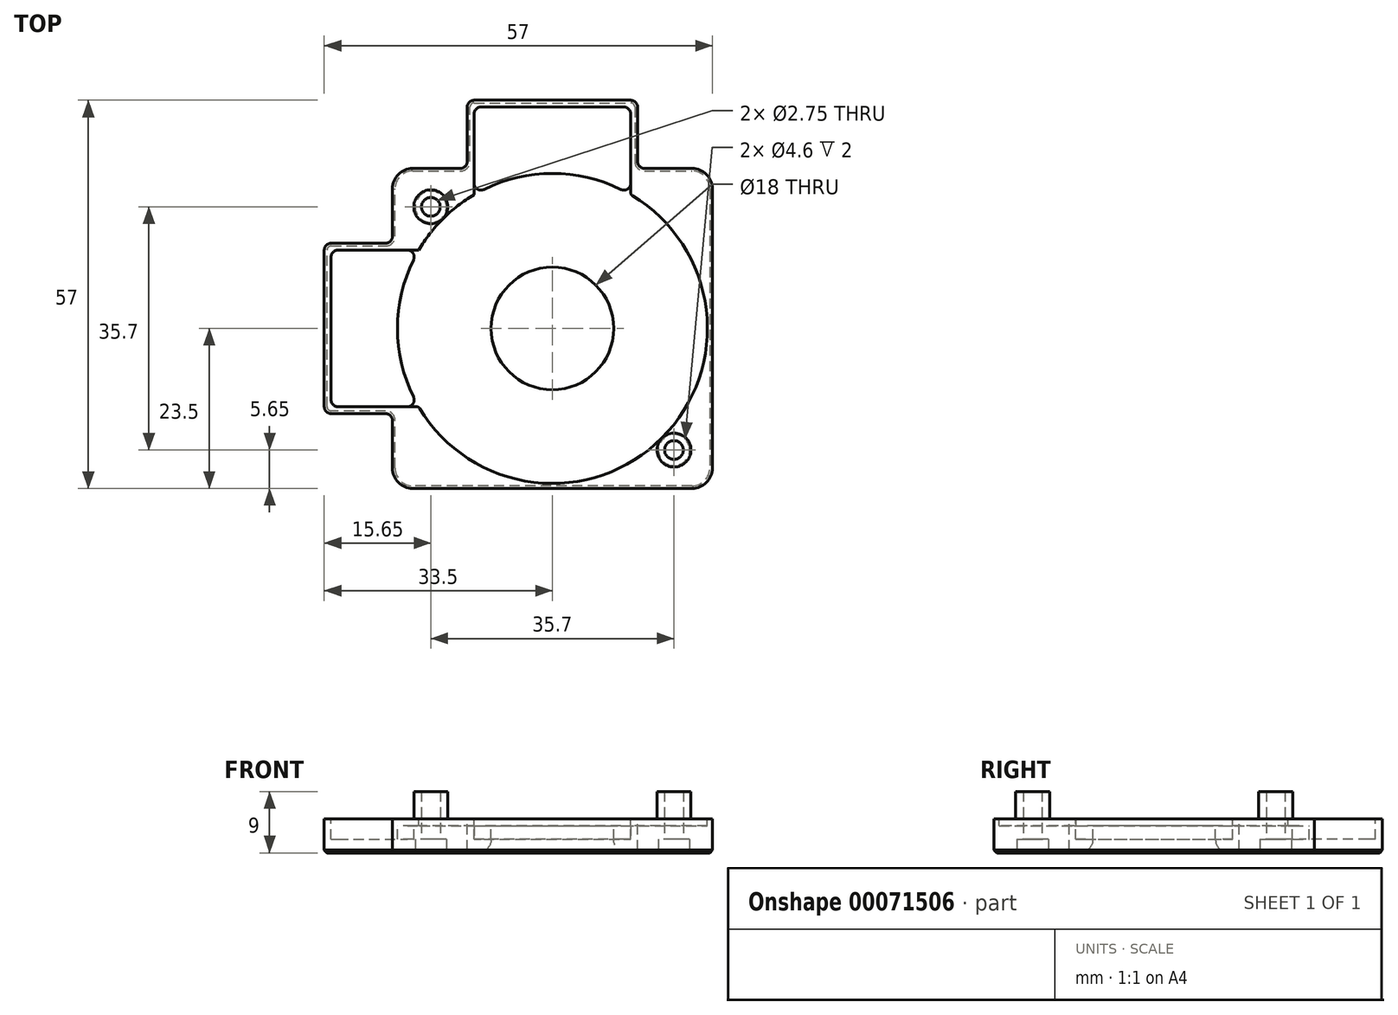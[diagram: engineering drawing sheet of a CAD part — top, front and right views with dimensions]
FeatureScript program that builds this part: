
annotation { "Feature Type Name" : "Feature", "Feature Type Description" : "" }
export const myFeature = defineFeature(function(context is Context, id is Id, definition is map)
    precondition{}
    {
        {
            var Q0;
            Q0=qCreatedBy(makeId("Top.planeOp"),FACE);
            var sketch = newSketch(context, id + "F0", { "sketchPlane" : qUnion([Q0])});
            skLineSegment(sketch, "E0.rect.bottom", {"start": v(23.5, 23.5) * mm, "end": v(-23.5, 23.5) * mm});
            skLineSegment(sketch, "E0.rect.top", {"start": v(23.5, -23.5) * mm, "end": v(12.5, -23.5) * mm});
            skLineSegment(sketch, "E0.rect.left", {"start": v(23.5, 23.5) * mm, "end": v(23.5, -23.5) * mm});
            skLineSegment(sketch, "E0.rect.right", {"start": v(-23.5, 23.5) * mm, "end": v(-23.5, 12.5) * mm});
            skPoint(sketch, "E0.rect.middle", {"position": v(0, 0) * mm});
            skPoint(sketch, "E1", {"position": v(17.85, 17.85) * mm});
            skLineSegment(sketch, "E2", {"start": v(-23.5, 12.5) * mm, "end": v(-33.5, 12.5) * mm});
            skLineSegment(sketch, "E3", {"start": v(-33.5, 12.5) * mm, "end": v(-33.5, -12.5) * mm});
            skLineSegment(sketch, "E4", {"start": v(-33.5, -12.5) * mm, "end": v(-23.5, -12.5) * mm});
            skLineSegment(sketch, "E5", {"start": v(-23.5, -23.5) * mm, "end": v(23.5, 23.5) * mm, "construction": true});
            skLineSegment(sketch, "E6.MirrorCS", {"start": v(12.5, -23.5) * mm, "end": v(12.5, -33.5) * mm});
            skLineSegment(sketch, "E7.MirrorCS", {"start": v(12.5, -33.5) * mm, "end": v(-12.5, -33.5) * mm});
            skLineSegment(sketch, "E8.MirrorCS", {"start": v(-12.5, -33.5) * mm, "end": v(-12.5, -23.5) * mm});
            skLineSegment(sketch, "E9.trimOffspring", {"start": v(-23.5, -12.5) * mm, "end": v(-23.5, -23.5) * mm});
            skLineSegment(sketch, "E10.trimOffspring", {"start": v(-12.5, -23.5) * mm, "end": v(-23.5, -23.5) * mm});
            skPoint(sketch, "E11", {"position": v(-17.85, -17.85) * mm});
            skSolve(sketch);
        }
        {
            var Q0;
            Q0=makeQuery(id+"F0.imprint","IMPRINT",FACE,{"disambiguationData":[TD([[makeQuery(id+"F0.imprint","IMPRINT",EDGE,{"derivedFrom":sQuery(id+"F0.wireOp",EDGE,"E0.rect.bottom")}),1.0]])]});
            extrude(context, id + "F1", {"entities" : qUnion([Q0]), "depth" : 5 * mm});
        }
        {
            var Q0;
            Q0=makeQuery(id+"F1.opExtrude","CAP_FACE",FACE,{"disambiguationData":[OSD([sQuery(id+"F0.wireOp",EDGE,"E0.rect.bottom"),sQuery(id+"F0.wireOp",EDGE,"E0.rect.top"),sQuery(id+"F0.wireOp",EDGE,"E0.rect.left"),sQuery(id+"F0.wireOp",EDGE,"E0.rect.right"),sQuery(id+"F0.wireOp",EDGE,"E2"),sQuery(id+"F0.wireOp",EDGE,"E3"),sQuery(id+"F0.wireOp",EDGE,"E4"),sQuery(id+"F0.wireOp",EDGE,"E6.MirrorCS"),sQuery(id+"F0.wireOp",EDGE,"E7.MirrorCS"),sQuery(id+"F0.wireOp",EDGE,"E8.MirrorCS"),sQuery(id+"F0.wireOp",EDGE,"E9.trimOffspring"),sQuery(id+"F0.wireOp",EDGE,"E10.trimOffspring")])],"isStart":true});
            var sketch = newSketch(context, id + "F2", { "sketchPlane" : qUnion([Q0])});
            skCircle(sketch, "E12", {"center": v(0, 0) * mm, "radius": 22.75 * mm});
            skSolve(sketch);
        }
        {
            var Q0;
            Q0=makeQuery(id+"F2.imprint","IMPRINT",FACE,{"disambiguationData":[TD([[makeQuery(id+"F2.imprint","IMPRINT",EDGE,{"derivedFrom":sQuery(id+"F2.wireOp",EDGE,"E12")}),1.0]])]});
            extrude(context, id + "F3", {"entities" : qUnion([Q0]), "operationType" : NewBodyOperationType.REMOVE, "oppositeDirection" : true, "depth" : 1 * mm});
        }
        {
            var Q0;
            Q0=makeQuery(id+"F0.imprint","IMPRINT",FACE,{"disambiguationData":[TD([[makeQuery(id+"F0.imprint","IMPRINT",EDGE,{"derivedFrom":sQuery(id+"F0.wireOp",EDGE,"E0.rect.bottom")}),1.0]])]});
            var sketch = newSketch(context, id + "F4", { "sketchPlane" : qUnion([Q0])});
            skPoint(sketch, "E13.0", {"position": v(-17.85, -17.85) * mm});
            skPoint(sketch, "E14.0", {"position": v(17.85, 17.85) * mm});
            skCircle(sketch, "E15", {"center": v(-17.85, -17.85) * mm, "radius": 2.5 * mm});
            skCircle(sketch, "E16", {"center": v(17.85, 17.85) * mm, "radius": 2.5 * mm});
            skLineSegment(sketch, "E17.0", {"start": v(-32.5, -11.5) * mm, "end": v(-19.63, -11.5) * mm});
            skLineSegment(sketch, "E17.1", {"start": v(-32.5, 11.5) * mm, "end": v(-32.5, -11.5) * mm});
            skLineSegment(sketch, "E17.2", {"start": v(-19.63, 11.5) * mm, "end": v(-32.5, 11.5) * mm});
            skCircle(sketch, "E18.0", {"center": v(0, 0) * mm, "radius": 22.75 * mm});
            skLineSegment(sketch, "E19.0", {"start": v(-11.5, -32.5) * mm, "end": v(-11.5, -19.63) * mm});
            skLineSegment(sketch, "E19.1", {"start": v(11.5, -32.5) * mm, "end": v(-11.5, -32.5) * mm});
            skLineSegment(sketch, "E19.2", {"start": v(11.5, -19.63) * mm, "end": v(11.5, -32.5) * mm});
            skSolve(sketch);
        }
        {
            var Q0;
            Q0=makeQuery(id+"F4.imprint","IMPRINT",FACE,{"disambiguationData":[TD([[makeQuery(id+"F4.imprint","IMPRINT",EDGE,{"derivedFrom":sQuery(id+"F4.wireOp",EDGE,"E15")}),1.0]])]});
            var Q1;
            Q1=makeQuery(id+"F4.imprint","IMPRINT",FACE,{"disambiguationData":[TD([[makeQuery(id+"F4.imprint","IMPRINT",EDGE,{"derivedFrom":sQuery(id+"F4.wireOp",EDGE,"E16")}),1.0]])]});
            var Q2;
            Q2=sQuery(id+"F4.wireOp",EDGE,"E15");
            var Q3;
            Q3=sQuery(id+"F4.wireOp",EDGE,"E16");
            extrude(context, id + "F5", {"entities" : qUnion([Q0, Q1]), "operationType" : NewBodyOperationType.ADD, "surfaceEntities" : qUnion([Q2, Q3]), "oppositeDirection" : true, "depth" : 4 * mm});
        }
        {
            var Q0;
            {var subQ0=sQuery(id+"F4.wireOp",EDGE,"E19.0");Q0=makeQuery(id+"F4.imprint","IMPRINT",FACE,{"disambiguationData":[TD([[makeQuery(id+"F4.imprint","IMPRINT",EDGE,{"derivedFrom":subQ0}),-1.0]])]});}
            var Q1;
            {var subQ0=sQuery(id+"F4.wireOp",EDGE,"E17.0");Q1=makeQuery(id+"F4.imprint","IMPRINT",FACE,{"disambiguationData":[TD([[makeQuery(id+"F4.imprint","IMPRINT",EDGE,{"derivedFrom":subQ0}),1.0]])]});}
            extrude(context, id + "F6", {"entities" : qUnion([Q0, Q1]), "operationType" : NewBodyOperationType.REMOVE, "depth" : 3 * mm});
        }
        {
            var Q0;
            Q0=makeQuery(id+"F3.boolean.opBoolean","COPY",FACE,{"derivedFrom":makeQuery(id+"F3.opExtrude","CAP_FACE",FACE,{"disambiguationData":[OSD([sQuery(id+"F2.wireOp",EDGE,"E12")])],"isStart":false})});
            var sketch = newSketch(context, id + "F7", { "sketchPlane" : qUnion([Q0])});
            skArc(sketch, "E20.0.0", {"start": v(-19.63, 11.5) * mm, "mid": v(-22.75, 0) * mm, "end": v(-19.63, -11.5) * mm});
            skArc(sketch, "E20.0.1", {"start": v(-19.63, -11.5) * mm, "mid": v(16.09, -16.09) * mm, "end": v(11.5, 19.63) * mm});
            skArc(sketch, "E20.0.2", {"start": v(11.5, 19.63) * mm, "mid": v(0, 22.75) * mm, "end": v(-11.5, 19.63) * mm});
            skArc(sketch, "E20.0.3", {"start": v(-11.5, 19.63) * mm, "mid": v(-16.09, 16.09) * mm, "end": v(-19.63, 11.5) * mm});
            skCircle(sketch, "E21", {"center": v(0, 0) * mm, "radius": 9 * mm});
            skSolve(sketch);
        }
        {
            var Q0;
            Q0=makeQuery(id+"F7.imprint","IMPRINT",FACE,{"disambiguationData":[TD([[makeQuery(id+"F7.imprint","IMPRINT",EDGE,{"derivedFrom":sQuery(id+"F7.wireOp",EDGE,"E21")}),1.0]])]});
            extrude(context, id + "F8", {"entities" : qUnion([Q0]), "operationType" : NewBodyOperationType.REMOVE, "endBound" : BoundingType.THROUGH_ALL, "oppositeDirection" : true, "depth" : 25 * mm});
        }
        {
            var Q0;
            Q0=makeQuery(id+"F1.opExtrude","SWEPT_EDGE",EDGE,{"disambiguationData":[OSD([sQuery(id+"F0.wireOp",EDGE,"E0.rect.bottom"),sQuery(id+"F0.wireOp",EDGE,"E0.rect.right")])]});
            var Q1;
            Q1=makeQuery(id+"F1.opExtrude","SWEPT_EDGE",EDGE,{"disambiguationData":[OSD([sQuery(id+"F0.wireOp",EDGE,"E0.rect.bottom"),sQuery(id+"F0.wireOp",EDGE,"E0.rect.left")])]});
            var Q2;
            Q2=makeQuery(id+"F1.opExtrude","SWEPT_EDGE",EDGE,{"disambiguationData":[OSD([sQuery(id+"F0.wireOp",EDGE,"E0.rect.top"),sQuery(id+"F0.wireOp",EDGE,"E0.rect.left")])]});
            var Q3;
            Q3=makeQuery(id+"F1.opExtrude","SWEPT_EDGE",EDGE,{"disambiguationData":[OSD([sQuery(id+"F0.wireOp",EDGE,"E9.trimOffspring"),sQuery(id+"F0.wireOp",EDGE,"E10.trimOffspring")])]});
            fillet(context, id + "F9", {"entities" : qUnion([Q0, Q1, Q2, Q3]), "radius" : 3 * mm, "tangentPropagation" : true, "allowEdgeOverflow" : false});
        }
        {
            var Q0;
            Q0=makeQuery(id+"F6.boolean.opBoolean","COPY",EDGE,{"derivedFrom":makeQuery(id+"F6.opExtrude","SWEPT_EDGE",EDGE,{"disambiguationData":[OSD([sQuery(id+"F4.wireOp",EDGE,"E17.0"),sQuery(id+"F4.wireOp",EDGE,"E17.1")])]})});
            var Q1;
            Q1=makeQuery(id+"F1.opExtrude","SWEPT_EDGE",EDGE,{"disambiguationData":[OSD([sQuery(id+"F0.wireOp",EDGE,"E2"),sQuery(id+"F0.wireOp",EDGE,"E3")])]});
            var Q2;
            Q2=makeQuery(id+"F6.boolean.opBoolean","COPY",EDGE,{"derivedFrom":makeQuery(id+"F6.opExtrude","SWEPT_EDGE",EDGE,{"disambiguationData":[OSD([sQuery(id+"F4.wireOp",EDGE,"E17.1"),sQuery(id+"F4.wireOp",EDGE,"E17.2")])]})});
            var Q3;
            Q3=makeQuery(id+"F1.opExtrude","SWEPT_EDGE",EDGE,{"disambiguationData":[OSD([sQuery(id+"F0.wireOp",EDGE,"E3"),sQuery(id+"F0.wireOp",EDGE,"E4")])]});
            var Q4;
            Q4=makeQuery(id+"F1.opExtrude","SWEPT_EDGE",EDGE,{"disambiguationData":[OSD([sQuery(id+"F0.wireOp",EDGE,"E7.MirrorCS"),sQuery(id+"F0.wireOp",EDGE,"E8.MirrorCS")])]});
            var Q5;
            Q5=makeQuery(id+"F1.opExtrude","SWEPT_EDGE",EDGE,{"disambiguationData":[OSD([sQuery(id+"F0.wireOp",EDGE,"E6.MirrorCS"),sQuery(id+"F0.wireOp",EDGE,"E7.MirrorCS")])]});
            var Q6;
            Q6=makeQuery(id+"F6.boolean.opBoolean","COPY",EDGE,{"derivedFrom":makeQuery(id+"F6.opExtrude","SWEPT_EDGE",EDGE,{"disambiguationData":[OSD([sQuery(id+"F4.wireOp",EDGE,"E19.0"),sQuery(id+"F4.wireOp",EDGE,"E19.1")])]})});
            var Q7;
            Q7=makeQuery(id+"F6.boolean.opBoolean","COPY",EDGE,{"derivedFrom":makeQuery(id+"F6.opExtrude","SWEPT_EDGE",EDGE,{"disambiguationData":[OSD([sQuery(id+"F4.wireOp",EDGE,"E19.1"),sQuery(id+"F4.wireOp",EDGE,"E19.2")])]})});
            var Q8;
            Q8=makeQuery(id+"F1.opExtrude","SWEPT_EDGE",EDGE,{"disambiguationData":[OSD([sQuery(id+"F0.wireOp",EDGE,"E4"),sQuery(id+"F0.wireOp",EDGE,"E9.trimOffspring")])]});
            var Q9;
            Q9=makeQuery(id+"F1.opExtrude","SWEPT_EDGE",EDGE,{"disambiguationData":[OSD([sQuery(id+"F0.wireOp",EDGE,"E0.rect.right"),sQuery(id+"F0.wireOp",EDGE,"E2")])]});
            var Q10;
            Q10=makeQuery(id+"F1.opExtrude","SWEPT_EDGE",EDGE,{"disambiguationData":[OSD([sQuery(id+"F0.wireOp",EDGE,"E8.MirrorCS"),sQuery(id+"F0.wireOp",EDGE,"E10.trimOffspring")])]});
            var Q11;
            Q11=makeQuery(id+"F1.opExtrude","SWEPT_EDGE",EDGE,{"disambiguationData":[OSD([sQuery(id+"F0.wireOp",EDGE,"E0.rect.top"),sQuery(id+"F0.wireOp",EDGE,"E6.MirrorCS")])]});
            var Q12;
            {var subQ0=sQuery(id+"F4.wireOp",EDGE,"E17.0");var subQ1=sQuery(id+"F4.wireOp",EDGE,"E18.0");Q12=makeQuery(id+"F6.boolean.opBoolean","COPY",EDGE,{"disambiguationData":[topologyDisambiguationEdgeConnected([makeQuery(id+"F6.opExtrude","SWEPT_FACE",FACE,{"disambiguationData":[OSD([subQ1]),TDD([makeQuery(id+"F4.imprint","IMPRINT",EDGE,{"disambiguationData":[TD([[makeQuery(id+"F4.imprint","INTERSECT",VERTEX,{"derivedFrom":[subQ0,subQ1]}),1.0]])],"derivedFrom":subQ1})])]})])],"derivedFrom":makeQuery(id+"F6.opExtrude","SWEPT_EDGE",EDGE,{"disambiguationData":[OSD([subQ0,subQ1])]})});}
            var Q13;
            {var subQ0=sQuery(id+"F4.wireOp",EDGE,"E17.2");var subQ1=sQuery(id+"F4.wireOp",EDGE,"E18.0");Q13=makeQuery(id+"F6.boolean.opBoolean","COPY",EDGE,{"disambiguationData":[topologyDisambiguationEdgeConnected([makeQuery(id+"F6.opExtrude","SWEPT_FACE",FACE,{"disambiguationData":[OSD([subQ1]),TDD([makeQuery(id+"F4.imprint","IMPRINT",EDGE,{"disambiguationData":[TD([[makeQuery(id+"F4.imprint","INTERSECT",VERTEX,{"derivedFrom":[sQuery(id+"F4.wireOp",EDGE,"E17.0"),subQ1]}),1.0]])],"derivedFrom":subQ1})])]})])],"derivedFrom":makeQuery(id+"F6.opExtrude","SWEPT_EDGE",EDGE,{"disambiguationData":[OSD([subQ0,subQ1])]})});}
            var Q14;
            {var subQ0=sQuery(id+"F4.wireOp",EDGE,"E18.0");var subQ1=sQuery(id+"F4.wireOp",EDGE,"E19.2");Q14=makeQuery(id+"F6.boolean.opBoolean","COPY",EDGE,{"disambiguationData":[topologyDisambiguationEdgeConnected([makeQuery(id+"F6.opExtrude","SWEPT_FACE",FACE,{"disambiguationData":[OSD([subQ0]),TDD([makeQuery(id+"F4.imprint","IMPRINT",EDGE,{"disambiguationData":[TD([[makeQuery(id+"F4.imprint","INTERSECT",VERTEX,{"derivedFrom":[subQ0,sQuery(id+"F4.wireOp",EDGE,"E19.0")]}),-1.0]])],"derivedFrom":subQ0})])]})])],"derivedFrom":makeQuery(id+"F6.opExtrude","SWEPT_EDGE",EDGE,{"disambiguationData":[OSD([subQ0,subQ1])]})});}
            var Q15;
            {var subQ0=sQuery(id+"F4.wireOp",EDGE,"E19.0");var subQ1=sQuery(id+"F4.wireOp",EDGE,"E18.0");Q15=makeQuery(id+"F6.boolean.opBoolean","COPY",EDGE,{"disambiguationData":[topologyDisambiguationEdgeConnected([makeQuery(id+"F6.opExtrude","SWEPT_FACE",FACE,{"disambiguationData":[OSD([subQ1]),TDD([makeQuery(id+"F4.imprint","IMPRINT",EDGE,{"disambiguationData":[TD([[makeQuery(id+"F4.imprint","INTERSECT",VERTEX,{"derivedFrom":[subQ1,subQ0]}),-1.0]])],"derivedFrom":subQ1})])]})])],"derivedFrom":makeQuery(id+"F6.opExtrude","SWEPT_EDGE",EDGE,{"disambiguationData":[OSD([subQ1,subQ0])]})});}
            fillet(context, id + "F10", {"entities" : qUnion([Q0, Q1, Q2, Q3, Q4, Q5, Q6, Q7, Q8, Q9, Q10, Q11, Q12, Q13, Q14, Q15]), "radius" : 1 * mm, "tangentPropagation" : true, "allowEdgeOverflow" : false});
        }
        {
            var Q0;
            {var subQ0=sQuery(id+"F4.wireOp",EDGE,"E17.0");Q0=makeQuery(id+"F6.boolean.opBoolean","COPY",EDGE,{"disambiguationData":[topologyDisambiguationEdgeConnected([makeQuery(id+"F3.boolean.opBoolean","COPY",FACE,{"derivedFrom":makeQuery(id+"F3.opExtrude","SWEPT_FACE",FACE,{"disambiguationData":[OSD([sQuery(id+"F2.wireOp",EDGE,"E12")])]})})])],"derivedFrom":makeQuery(id+"F6.opExtrude","SWEPT_EDGE",EDGE,{"disambiguationData":[OSD([subQ0,sQuery(id+"F4.wireOp",EDGE,"E18.0")])]})});}
            var Q1;
            {var subQ0=sQuery(id+"F4.wireOp",EDGE,"E19.0");Q1=makeQuery(id+"F6.boolean.opBoolean","COPY",EDGE,{"disambiguationData":[topologyDisambiguationEdgeConnected([makeQuery(id+"F3.boolean.opBoolean","COPY",FACE,{"derivedFrom":makeQuery(id+"F3.opExtrude","SWEPT_FACE",FACE,{"disambiguationData":[OSD([sQuery(id+"F2.wireOp",EDGE,"E12")])]})})])],"derivedFrom":makeQuery(id+"F6.opExtrude","SWEPT_EDGE",EDGE,{"disambiguationData":[OSD([sQuery(id+"F4.wireOp",EDGE,"E18.0"),subQ0])]})});}
            var Q2;
            {var subQ0=sQuery(id+"F4.wireOp",EDGE,"E19.2");Q2=makeQuery(id+"F6.boolean.opBoolean","COPY",EDGE,{"disambiguationData":[topologyDisambiguationEdgeConnected([makeQuery(id+"F3.boolean.opBoolean","COPY",FACE,{"derivedFrom":makeQuery(id+"F3.opExtrude","SWEPT_FACE",FACE,{"disambiguationData":[OSD([sQuery(id+"F2.wireOp",EDGE,"E12")])]})})])],"derivedFrom":makeQuery(id+"F6.opExtrude","SWEPT_EDGE",EDGE,{"disambiguationData":[OSD([sQuery(id+"F4.wireOp",EDGE,"E18.0"),subQ0])]})});}
            var Q3;
            {var subQ0=sQuery(id+"F4.wireOp",EDGE,"E17.2");Q3=makeQuery(id+"F6.boolean.opBoolean","COPY",EDGE,{"disambiguationData":[topologyDisambiguationEdgeConnected([makeQuery(id+"F3.boolean.opBoolean","COPY",FACE,{"derivedFrom":makeQuery(id+"F3.opExtrude","SWEPT_FACE",FACE,{"disambiguationData":[OSD([sQuery(id+"F2.wireOp",EDGE,"E12")])]})})])],"derivedFrom":makeQuery(id+"F6.opExtrude","SWEPT_EDGE",EDGE,{"disambiguationData":[OSD([subQ0,sQuery(id+"F4.wireOp",EDGE,"E18.0")])]})});}
            fillet(context, id + "F11", {"entities" : qUnion([Q0, Q1, Q2, Q3]), "radius" : .5 * mm, "tangentPropagation" : true, "allowEdgeOverflow" : false});
        }
        {
            var Q0;
            Q0=makeQuery(id+"F1.opExtrude","CAP_FACE",FACE,{"disambiguationData":[OSD([sQuery(id+"F0.wireOp",EDGE,"E0.rect.bottom"),sQuery(id+"F0.wireOp",EDGE,"E0.rect.top"),sQuery(id+"F0.wireOp",EDGE,"E0.rect.left"),sQuery(id+"F0.wireOp",EDGE,"E0.rect.right"),sQuery(id+"F0.wireOp",EDGE,"E2"),sQuery(id+"F0.wireOp",EDGE,"E3"),sQuery(id+"F0.wireOp",EDGE,"E4"),sQuery(id+"F0.wireOp",EDGE,"E6.MirrorCS"),sQuery(id+"F0.wireOp",EDGE,"E7.MirrorCS"),sQuery(id+"F0.wireOp",EDGE,"E8.MirrorCS"),sQuery(id+"F0.wireOp",EDGE,"E9.trimOffspring"),sQuery(id+"F0.wireOp",EDGE,"E10.trimOffspring")])],"isStart":false});
            var sketch = newSketch(context, id + "F12", { "sketchPlane" : qUnion([Q0])});
            skPoint(sketch, "E22.0", {"position": v(17.85, 17.85) * mm});
            skPoint(sketch, "E23.0", {"position": v(-17.85, -17.85) * mm});
            skSolve(sketch);
        }
        {
            var Q0;
            Q0=sQuery(id+"F12.wireOp",VERTEX,"E23.0");
            var Q1;
            Q1=sQuery(id+"F12.wireOp",VERTEX,"E22.0");
            var Q2;
            Q2=makeQuery(id+"F1.opExtrude","SWEPT_BODY",BODY,{"disambiguationData":[OSD([sQuery(id+"F0.wireOp",EDGE,"E0.rect.bottom"),sQuery(id+"F0.wireOp",EDGE,"E0.rect.top"),sQuery(id+"F0.wireOp",EDGE,"E0.rect.left"),sQuery(id+"F0.wireOp",EDGE,"E0.rect.right"),sQuery(id+"F0.wireOp",EDGE,"E2"),sQuery(id+"F0.wireOp",EDGE,"E3"),sQuery(id+"F0.wireOp",EDGE,"E4"),sQuery(id+"F0.wireOp",EDGE,"E6.MirrorCS"),sQuery(id+"F0.wireOp",EDGE,"E7.MirrorCS"),sQuery(id+"F0.wireOp",EDGE,"E8.MirrorCS"),sQuery(id+"F0.wireOp",EDGE,"E9.trimOffspring"),sQuery(id+"F0.wireOp",EDGE,"E10.trimOffspring")])]});
            hole(context, id + "F13", {"style" : HoleStyle.C_BORE, "holeDiameter" : 2.75 * mm, "cBoreDiameter" : 4.6 * mm, "cBoreDepth" : 2 * mm, "endStyle" : HoleEndStyle.THROUGH, "locations" : qUnion([Q0, Q1]), "scope" : qUnion([Q2])});
        }
        {
            var Q0;
            Q0=makeQuery(id+"F8.boolean.opBoolean","INTERSECT",EDGE,{"derivedFrom":[makeQuery(id+"F1.opExtrude","CAP_FACE",FACE,{"disambiguationData":[OSD([sQuery(id+"F0.wireOp",EDGE,"E0.rect.bottom"),sQuery(id+"F0.wireOp",EDGE,"E0.rect.top"),sQuery(id+"F0.wireOp",EDGE,"E0.rect.left"),sQuery(id+"F0.wireOp",EDGE,"E0.rect.right"),sQuery(id+"F0.wireOp",EDGE,"E2"),sQuery(id+"F0.wireOp",EDGE,"E3"),sQuery(id+"F0.wireOp",EDGE,"E4"),sQuery(id+"F0.wireOp",EDGE,"E6.MirrorCS"),sQuery(id+"F0.wireOp",EDGE,"E7.MirrorCS"),sQuery(id+"F0.wireOp",EDGE,"E8.MirrorCS"),sQuery(id+"F0.wireOp",EDGE,"E9.trimOffspring"),sQuery(id+"F0.wireOp",EDGE,"E10.trimOffspring")])],"isStart":false}),makeQuery(id+"F8.opExtrude","SWEPT_FACE",FACE,{"disambiguationData":[OSD([sQuery(id+"F7.wireOp",EDGE,"E21")])]})]});
            var Q1;
            Q1=makeQuery(id+"F8.boolean.opBoolean","COPY",EDGE,{"derivedFrom":makeQuery(id+"F8.opExtrude","CAP_EDGE",EDGE,{"disambiguationData":[OSD([sQuery(id+"F7.wireOp",EDGE,"E21")])],"isStart":true})});
            fillet(context, id + "F14", {"entities" : qUnion([Q0, Q1]), "radius" : 2 * mm, "tangentPropagation" : true, "allowEdgeOverflow" : false});
        }
        {
            var Q0;
            Q0=makeQuery(id+"F1.opExtrude","CAP_EDGE",EDGE,{"disambiguationData":[OSD([sQuery(id+"F0.wireOp",EDGE,"E3")])],"isStart":false});
            chamfer(context, id + "F15", {"entities" : qUnion([Q0]), "width" : .4 * mm, "tangentPropagation" : true});
        }
        {
            var Q0;
            Q0=makeQuery(id+"F1.opExtrude","SWEPT_BODY",BODY,{"disambiguationData":[OSD([sQuery(id+"F0.wireOp",EDGE,"E0.rect.bottom"),sQuery(id+"F0.wireOp",EDGE,"E0.rect.top"),sQuery(id+"F0.wireOp",EDGE,"E0.rect.left"),sQuery(id+"F0.wireOp",EDGE,"E0.rect.right"),sQuery(id+"F0.wireOp",EDGE,"E2"),sQuery(id+"F0.wireOp",EDGE,"E3"),sQuery(id+"F0.wireOp",EDGE,"E4"),sQuery(id+"F0.wireOp",EDGE,"E6.MirrorCS"),sQuery(id+"F0.wireOp",EDGE,"E7.MirrorCS"),sQuery(id+"F0.wireOp",EDGE,"E8.MirrorCS"),sQuery(id+"F0.wireOp",EDGE,"E9.trimOffspring"),sQuery(id+"F0.wireOp",EDGE,"E10.trimOffspring")])]});
            var Q1;
            Q1=makeQuery(id+"F1.opExtrude","CAP_EDGE",EDGE,{"disambiguationData":[OSD([sQuery(id+"F0.wireOp",EDGE,"E7.MirrorCS")])],"isStart":true});
            transform(context, id + "F16", {"entities" : qUnion([Q0]), "transformType" : TransformType.ROTATION, "transformAxis" : qUnion([Q1]), "angle" : 180 * degree, "makeCopy" : false});
        }
        {
            var Q0;
            Q0=makeQuery(id+"F1.opExtrude","SWEPT_BODY",BODY,{"disambiguationData":[OSD([sQuery(id+"F0.wireOp",EDGE,"E0.rect.bottom"),sQuery(id+"F0.wireOp",EDGE,"E0.rect.top"),sQuery(id+"F0.wireOp",EDGE,"E0.rect.left"),sQuery(id+"F0.wireOp",EDGE,"E0.rect.right"),sQuery(id+"F0.wireOp",EDGE,"E2"),sQuery(id+"F0.wireOp",EDGE,"E3"),sQuery(id+"F0.wireOp",EDGE,"E4"),sQuery(id+"F0.wireOp",EDGE,"E6.MirrorCS"),sQuery(id+"F0.wireOp",EDGE,"E7.MirrorCS"),sQuery(id+"F0.wireOp",EDGE,"E8.MirrorCS"),sQuery(id+"F0.wireOp",EDGE,"E9.trimOffspring"),sQuery(id+"F0.wireOp",EDGE,"E10.trimOffspring")])]});
            var Q1;
            Q1=qCreatedBy(makeId("Front.planeOp"),FACE);
            transform(context, id + "F17", {"entities" : qUnion([Q0]), "transformType" : TransformType.TRANSLATION_DISTANCE, "transformDirection" : qUnion([Q1]), "distance" : 50 * mm, "oppositeDirection" : true, "makeCopy" : false});
        }
    });
